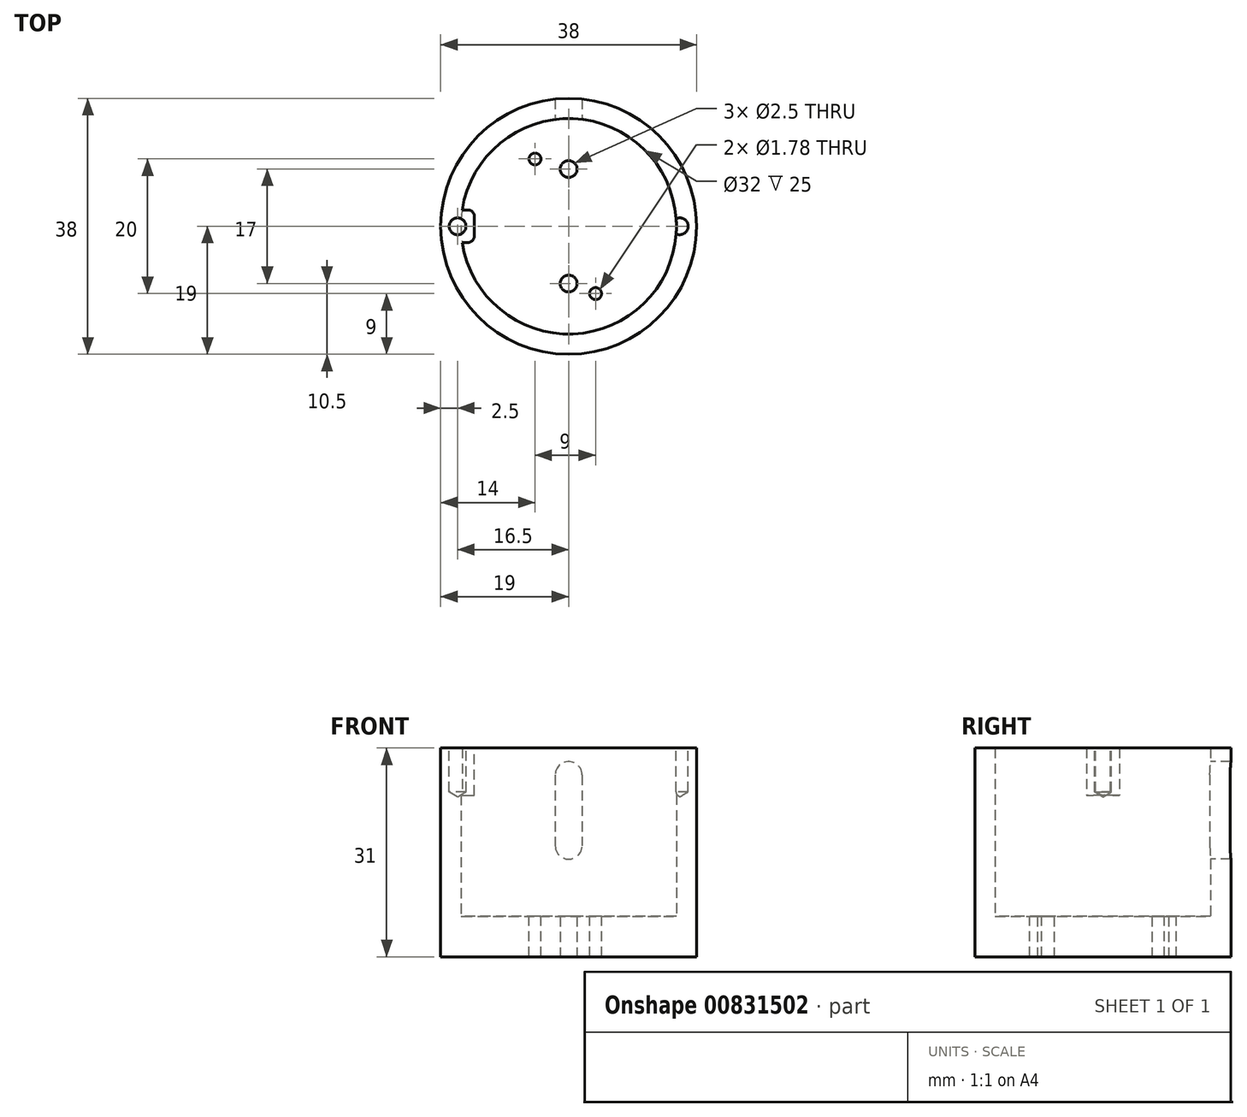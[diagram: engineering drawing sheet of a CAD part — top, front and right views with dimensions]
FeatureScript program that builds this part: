
annotation { "Feature Type Name" : "Feature", "Feature Type Description" : "" }
export const myFeature = defineFeature(function(context is Context, id is Id, definition is map)
    precondition{}
    {
        {
            var Q0;
            Q0=qCreatedBy(makeId("Top.planeOp"),FACE);
            var sketch = newSketch(context, id + "F0", { "sketchPlane" : qUnion([Q0])});
            skCircle(sketch, "E0", {"center": v(0, 0) * mm, "radius": 19 * mm});
            skSolve(sketch);
        }
        {
            var Q0;
            Q0 = qSketchRegion(id + "F0", true);
            extrude(context, id + "F1", {"entities" : qUnion([Q0]), "depth" : 6 * mm, "offsetDistance" : 25 * mm});
        }
        {
            var Q0;
            Q0=makeQuery(id+"F1.opExtrude","CAP_FACE",FACE,{"disambiguationData":[OSD([sQuery(id+"F0.wireOp",EDGE,"E0")])],"isStart":false});
            var sketch = newSketch(context, id + "F2", { "sketchPlane" : qUnion([Q0])});
            skCircle(sketch, "E1.0", {"center": v(0, 0) * mm, "radius": 19 * mm});
            skCircle(sketch, "E2", {"center": v(0, 0) * mm, "radius": 16 * mm});
            skSolve(sketch);
        }
        {
            var Q0;
            Q0 = qSketchRegion(id + "F2", true);
            extrude(context, id + "F3", {"entities" : qUnion([Q0]), "operationType" : NewBodyOperationType.ADD, "depth" : (31 - 6) * mm, "offsetDistance" : 25 * mm});
        }
        {
            var Q0;
            Q0=makeQuery(id+"F1.opExtrude","CAP_FACE",FACE,{"disambiguationData":[OSD([sQuery(id+"F0.wireOp",EDGE,"E0")])],"isStart":true});
            var sketch = newSketch(context, id + "F4", { "sketchPlane" : qUnion([Q0])});
            skLineSegment(sketch, "E3", {"start": v(0, 8.5) * mm, "end": v(0, -8.5) * mm, "construction": true});
            skSolve(sketch);
        }
        {
            var Q0;
            Q0=sQuery(id+"F4.wireOp",VERTEX,"E3.end");
            var Q1;
            Q1=sQuery(id+"F4.wireOp",VERTEX,"E3.start");
            var Q2;
            Q2=makeQuery(id+"F1.opExtrude","SWEPT_BODY",BODY,{"disambiguationData":[OSD([sQuery(id+"F0.wireOp",EDGE,"E0")])]});
            hole(context, id + "F5", {"style" : HoleStyle.SIMPLE, "endStyle" : HoleEndStyle.THROUGH, "standardTappedOrClearance" : lookupTablePath({ "standard" : "ISO", "engagement" : "75%", "pitch" : "0.5 mm", "size" : "M3", "type" : "Tapped" }), "standardBlindInLast" : lookupTablePath({ "standard" : "ISO", "engagement" : "75%", "pitch" : "0.5 mm", "size" : "M3", "type" : "Tapped" }), "holeDiameter" : 2.5 * mm, "majorDiameter" : 3 * mm, "showTappedDepth" : true, "isTappedThrough" : true, "tappedDepth" : 5 * mm, "tapClearance" : 3, "startFromSketch" : true, "locations" : qUnion([Q0, Q1]), "scope" : qUnion([Q2])});
        }
        {
            var Q0;
            Q0=makeQuery(id+"F1.opExtrude","CAP_FACE",FACE,{"disambiguationData":[OSD([sQuery(id+"F0.wireOp",EDGE,"E0")])],"isStart":false});
            var sketch = newSketch(context, id + "F6", { "sketchPlane" : qUnion([Q0])});
            skLineSegment(sketch, "E4", {"start": v(0, 0) * mm, "end": v(0, 10) * mm, "construction": true});
            skLineSegment(sketch, "E5", {"start": v(0, 10) * mm, "end": v(-5, 10) * mm, "construction": true});
            skLineSegment(sketch, "E6", {"start": v(0, 0) * mm, "end": v(0, -10) * mm, "construction": true});
            skLineSegment(sketch, "E7", {"start": v(0, -10) * mm, "end": v(4, -10) * mm, "construction": true});
            skSolve(sketch);
        }
        {
            var Q0;
            Q0=sQuery(id+"F6.wireOp",VERTEX,"E5.end");
            var Q1;
            Q1=sQuery(id+"F6.wireOp",VERTEX,"E7.end");
            var Q2;
            Q2=makeQuery(id+"F1.opExtrude","SWEPT_BODY",BODY,{"disambiguationData":[OSD([sQuery(id+"F0.wireOp",EDGE,"E0")])]});
            hole(context, id + "F7", {"style" : HoleStyle.SIMPLE, "endStyle" : HoleEndStyle.THROUGH, "standardTappedOrClearance" : lookupTablePath({ "standard" : "ANSI", "engagement" : "75%", "pitch" : "56 tpi", "size" : "#2", "type" : "Tapped" }), "standardBlindInLast" : lookupTablePath({ "standard" : "ANSI", "engagement" : "75%", "pitch" : "56 tpi", "size" : "#2", "type" : "Tapped" }), "holeDiameter" : 1.78 * mm, "majorDiameter" : 2.18 * mm, "showTappedDepth" : true, "isTappedThrough" : true, "tappedDepth" : 5 * mm, "tapClearance" : 3, "startFromSketch" : true, "locations" : qUnion([Q0, Q1]), "scope" : qUnion([Q2])});
        }
        {
            var Q0;
            Q0=qCreatedBy(makeId("Front.planeOp"),FACE);
            var sketch = newSketch(context, id + "F8", { "sketchPlane" : qUnion([Q0])});
            skLineSegment(sketch, "E8.bottom", {"start": v(-2, 16.5) * mm, "end": v(2, 16.5) * mm, "construction": true});
            skLineSegment(sketch, "E8.top", {"start": v(-2, 27) * mm, "end": v(2, 27) * mm, "construction": true});
            skLineSegment(sketch, "E8.left", {"start": v(-2, 27) * mm, "end": v(-2, 16.5) * mm});
            skLineSegment(sketch, "E8.right", {"start": v(2, 27) * mm, "end": v(2, 16.5) * mm});
            skLineSegment(sketch, "E9", {"start": v(0, 0) * mm, "end": v(0, 27) * mm, "construction": true});
            skArc(sketch, "E10", {"start": v(-2, 27) * mm, "mid": v(0, 29) * mm, "end": v(2, 27) * mm});
            skArc(sketch, "E11", {"start": v(-2, 16.5) * mm, "mid": v(0, 14.5) * mm, "end": v(2, 16.5) * mm});
            skSolve(sketch);
        }
        {
            var Q0;
            Q0 = qSketchRegion(id + "F8", true);
            extrude(context, id + "F9", {"entities" : qUnion([Q0]), "operationType" : NewBodyOperationType.REMOVE, "endBound" : BoundingType.THROUGH_ALL, "oppositeDirection" : true, "depth" : 25 * mm, "offsetDistance" : 25 * mm});
        }
        {
            var Q0;
            Q0=makeQuery(id+"F3.opExtrude","CAP_FACE",FACE,{"disambiguationData":[OSD([sQuery(id+"F2.wireOp",EDGE,"E1.0"),sQuery(id+"F2.wireOp",EDGE,"E2")])],"isStart":false});
            var sketch = newSketch(context, id + "F10", { "sketchPlane" : qUnion([Q0])});
            skCircle(sketch, "E12.0", {"center": v(0, 0) * mm, "radius": 19 * mm, "construction": true});
            skLineSegment(sketch, "E13.bottom", {"start": v(-18.84, 2.42) * mm, "end": v(-14, 2.42) * mm});
            skLineSegment(sketch, "E13.top", {"start": v(-18.84, -2.42) * mm, "end": v(-14, -2.42) * mm});
            skLineSegment(sketch, "E13.left", {"start": v(-18.84, 2.42) * mm, "end": v(-18.84, -2.42) * mm});
            skLineSegment(sketch, "E13.right", {"start": v(-14, 2.42) * mm, "end": v(-14, -2.42) * mm});
            skCircle(sketch, "E14", {"center": v(0, 0) * mm, "radius": 14 * mm, "construction": true});
            skSolve(sketch);
        }
        {
            var Q0;
            Q0 = qSketchRegion(id + "F10", true);
            extrude(context, id + "F11", {"entities" : qUnion([Q0]), "operationType" : NewBodyOperationType.ADD, "oppositeDirection" : true, "depth" : 7 * mm, "offsetDistance" : 25 * mm});
        }
        {
            var Q0;
            Q0=makeQuery(id+"F3.opExtrude","CAP_FACE",FACE,{"disambiguationData":[OSD([sQuery(id+"F2.wireOp",EDGE,"E1.0"),sQuery(id+"F2.wireOp",EDGE,"E2")])],"isStart":false});
            var sketch = newSketch(context, id + "F12", { "sketchPlane" : qUnion([Q0])});
            skLineSegment(sketch, "E15", {"start": v(-16.5, 0) * mm, "end": v(16.5, 0) * mm, "construction": true});
            skSolve(sketch);
        }
        {
            var Q0;
            Q0=sQuery(id+"F12.wireOp",VERTEX,"E15.start");
            var Q1;
            Q1=sQuery(id+"F12.wireOp",VERTEX,"E15.end");
            var Q2;
            Q2=makeQuery(id+"F1.opExtrude","SWEPT_BODY",BODY,{"disambiguationData":[OSD([sQuery(id+"F0.wireOp",EDGE,"E0")])]});
            hole(context, id + "F13", {"style" : HoleStyle.SIMPLE, "endStyle" : HoleEndStyle.BLIND, "standardTappedOrClearance" : lookupTablePath({ "standard" : "ISO", "engagement" : "75%", "pitch" : "0.5 mm", "size" : "M3", "type" : "Tapped" }), "standardBlindInLast" : lookupTablePath({ "standard" : "ISO", "engagement" : "75%", "pitch" : "0.5 mm", "size" : "M3", "type" : "Tapped" }), "holeDiameter" : 2.5 * mm, "majorDiameter" : 3 * mm, "showTappedDepth" : true, "holeDepth" : 6.5 * mm, "isTappedThrough" : true, "tappedDepth" : 5 * mm, "tapClearance" : 3, "startFromSketch" : true, "locations" : qUnion([Q0, Q1]), "scope" : qUnion([Q2])});
        }
        {
            var Q0;
            Q0=makeQuery(id+"F11.opExtrude","SWEPT_EDGE",EDGE,{"disambiguationData":[OSD([sQuery(id+"F10.wireOp",EDGE,"E13.bottom"),sQuery(id+"F10.wireOp",EDGE,"E13.right")])]});
            var Q1;
            Q1=makeQuery(id+"F11.opExtrude","SWEPT_EDGE",EDGE,{"disambiguationData":[OSD([sQuery(id+"F10.wireOp",EDGE,"E13.top"),sQuery(id+"F10.wireOp",EDGE,"E13.right")])]});
            var Q2;
            Q2=makeQuery(id+"FECqVo5kZtgYw6F_1.1.F11.opExtrude","SWEPT_EDGE",EDGE,{"disambiguationData":[OSD([sQuery(id+"F10.wireOp",EDGE,"E13.top"),sQuery(id+"F10.wireOp",EDGE,"E13.right")])]});
            var Q3;
            Q3=makeQuery(id+"FECqVo5kZtgYw6F_1.1.F11.opExtrude","SWEPT_EDGE",EDGE,{"disambiguationData":[OSD([sQuery(id+"F10.wireOp",EDGE,"E13.bottom"),sQuery(id+"F10.wireOp",EDGE,"E13.right")])]});
            fillet(context, id + "F14", {"entities" : qUnion([Q0, Q1, Q2, Q3]), "radius" : 1 * mm, "tangentPropagation" : true, "allowEdgeOverflow" : false});
        }
    });
